# Revit family: Accessory-Handshower_Holder-KOHLER-RENEW-K-98347T
name_source: partatom
category: Specialty Equipment
revit_build: Autodesk Revit 2017 (Build: 20160225_1515(x64)
units: mm (PartAtom-declared; Revit-internal decimal feet)

## family parameters
Cut with Voids When Loaded = No
Host = Face
OmniClass Number = 23.31.25.00
OmniClass Title = Toilet and Bath Specialties
Part Type = Normal
Room Calculation Point = No
Round Connector Dimension = Use Diameter
Shared = No

## types (3) — shared parameters
ADA Compliant = No
Assembly Code = C1030200
Date Modified = 08/27/2020
Default Elevation = 42"
Description = FIXED WALL MOUNT BRACKET
Height = 2 5/16"
Length = 1 7/8"
Manufacturer = KOHLER Co.
Master Format 2014 = 10 28 00
Master Format 2014 Name = Toilet, Bath, and Laundry Accessories
Material = Premium Metal Construction
Product Documentation Link = https://files.kohler.com.cn
Product Name = RENEW
Product Page URL = https://www.kohler.com.cn
URL = http://www.kohler.com.cn
WaterSense Certified = No
Width = 2"

## per-type parameters (varying)
| type | Finish | Model | Type |
| CP-Polished chrome | Kohler-Metal-CP-Polished_Chrome | K-98347T-CP | 1 |
| 2BL-Primitive black | Kohler-Metal-2BL-Original_Black | K-98347T-2BL | 2 |
| BL-Primary color black | Kohler-Metal-BL-Matte_Black | K-98347T-BL | 3 |

## geometry (parser evidence)
native form markers: Sweep x6
no freeform markers — native parametric forms only
